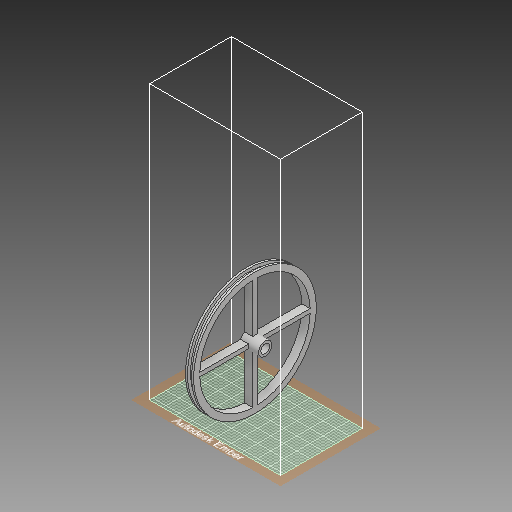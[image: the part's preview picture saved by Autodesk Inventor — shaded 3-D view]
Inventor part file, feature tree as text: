
AUTODESK INVENTOR PART (.ipt)
format: ipt  version: 2018 (Build 220112000, 112)  size: 338,944 bytes
history: native  units: mm
features: extrude x8, sketch x8, pattern_circular x1
ambient origin geometry x8: Origin, YZ Plane, XZ Plane, XY Plane, X Axis, Y Axis, Z Axis, Center Point
bodies: Solid1 (feature_tree)
feature tree (17):
  extrude  "Extrusion1"  Depth=2.0mm TaperAngle=0.0deg
  extrude  "Extrusion2"  Depth=1.0mm TaperAngle=0.0deg
  extrude  "Extrusion3"  Depth=1.0mm TaperAngle=0.0deg
  extrude  "Extrusion4"  Depth=10.0mm TaperAngle=0.0deg
  extrude  "Extrusion5"  Depth=6.5mm
  extrude  "Extrusion6"  Depth=1.0mm
  pattern_circular  "Circular Pattern1"  Count=4 Angle=360.0deg
  extrude  "Extrusion7"  Depth=5.0mm TaperAngle=0.0deg
  extrude  "Extrusion8"  Depth=9.0mm
  sketch  "Sketch1"  dims[d0=57.0mm d1=2.0mm d2=0.0mm]
  sketch  "Sketch2"  dims[d3=60.0mm d4=1.0mm d5=0.0mm]
  sketch  "Sketch3"  dims[d6=60.0mm d7=1.0mm d8=0.0mm]
  sketch  "Sketch4"  dims[d9=54.0mm d10=10.0mm d11=0.0mm]
  sketch  "Sketch5"  dims[d12=4.25mm d13=6.5mm]
  sketch  "Sketch6"  dims[d14=4.0mm d15=0.0mm d16=1.0mm]
  sketch  "Sketch7"  dims[d17=2.0mm]
  sketch  "Sketch8"  dims[d18=4.0mm d19=0.0mm d20=40.0mm d21=360.0deg d23=5.0mm d24=0.0mm d25=9.0mm d26=4.25mm d27=9.0mm d28=0.0mm]
